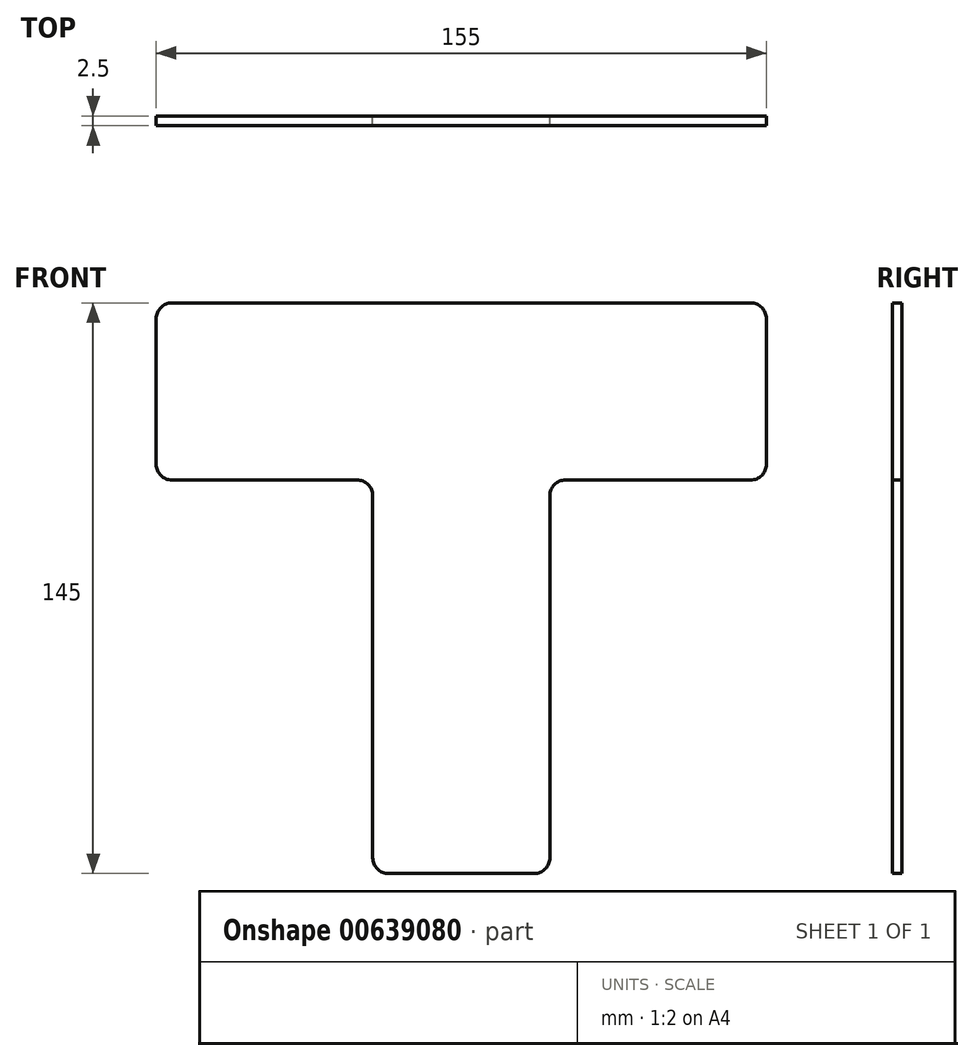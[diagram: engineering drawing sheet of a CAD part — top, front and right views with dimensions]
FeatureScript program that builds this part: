
annotation { "Feature Type Name" : "Feature", "Feature Type Description" : "" }
export const myFeature = defineFeature(function(context is Context, id is Id, definition is map)
    precondition{}
    {
        {
            var Q0;
            Q0=qCreatedBy(makeId("Front.planeOp"),FACE);
            var sketch = newSketch(context, id + "F0", { "sketchPlane" : qUnion([Q0])});
            skLineSegment(sketch, "E0.bottom", {"start": v(73.5, 22.5) * mm, "end": v(-73.5, 22.5) * mm});
            skLineSegment(sketch, "E0.top", {"start": v(77.5, -22.5) * mm, "end": v(22.5, -22.5) * mm});
            skLineSegment(sketch, "E0.left", {"start": v(77.5, 18.5) * mm, "end": v(77.5, -18.5) * mm});
            skLineSegment(sketch, "E0.right", {"start": v(-77.5, 18.5) * mm, "end": v(-77.5, -18.5) * mm});
            skPoint(sketch, "E0.middle", {"position": v(0, 0) * mm});
            skLineSegment(sketch, "E1", {"start": v(73.5, -22.5) * mm, "end": v(26.5, -22.5) * mm});
            skLineSegment(sketch, "E2", {"start": v(22.5, -26.5) * mm, "end": v(22.5, -118.5) * mm});
            skLineSegment(sketch, "E3", {"start": v(18.5, -122.5) * mm, "end": v(-18.5, -122.5) * mm});
            skLineSegment(sketch, "E4", {"start": v(-22.5, -118.5) * mm, "end": v(-22.5, -26.5) * mm});
            skLineSegment(sketch, "E5", {"start": v(-22.5, -22.5) * mm, "end": v(-77.5, -22.5) * mm});
            skLineSegment(sketch, "E6.trimOffspring", {"start": v(-26.5, -22.5) * mm, "end": v(-73.5, -22.5) * mm});
            skPoint(sketch, "E7.visualSharp", {"position": v(-77.5, 22.5) * mm});
            skArc(sketch, "E7.filletArc", {"start": v(-73.5, 22.5) * mm, "mid": v(-76.33, 21.33) * mm, "end": v(-77.5, 18.5) * mm});
            skPoint(sketch, "E8.visualSharp", {"position": v(-77.5, -22.5) * mm});
            skArc(sketch, "E8.filletArc", {"start": v(-77.5, -18.5) * mm, "mid": v(-76.33, -21.33) * mm, "end": v(-73.5, -22.5) * mm});
            skPoint(sketch, "E9.visualSharp", {"position": v(77.5, -22.5) * mm});
            skArc(sketch, "E9.filletArc", {"start": v(73.5, -22.5) * mm, "mid": v(76.33, -21.33) * mm, "end": v(77.5, -18.5) * mm});
            skPoint(sketch, "E10.visualSharp", {"position": v(77.5, 22.5) * mm});
            skArc(sketch, "E10.filletArc", {"start": v(77.5, 18.5) * mm, "mid": v(76.33, 21.33) * mm, "end": v(73.5, 22.5) * mm});
            skPoint(sketch, "E11.visualSharp", {"position": v(22.5, -22.5) * mm});
            skArc(sketch, "E11.filletArc", {"start": v(26.5, -22.5) * mm, "mid": v(23.67, -23.67) * mm, "end": v(22.5, -26.5) * mm});
            skPoint(sketch, "E12.visualSharp", {"position": v(-22.5, -22.5) * mm});
            skArc(sketch, "E12.filletArc", {"start": v(-22.5, -26.5) * mm, "mid": v(-23.67, -23.67) * mm, "end": v(-26.5, -22.5) * mm});
            skPoint(sketch, "E13.visualSharp", {"position": v(-22.5, -122.5) * mm});
            skArc(sketch, "E13.filletArc", {"start": v(-22.5, -118.5) * mm, "mid": v(-21.33, -121.33) * mm, "end": v(-18.5, -122.5) * mm});
            skPoint(sketch, "E14.visualSharp", {"position": v(22.5, -122.5) * mm});
            skArc(sketch, "E14.filletArc", {"start": v(18.5, -122.5) * mm, "mid": v(21.33, -121.33) * mm, "end": v(22.5, -118.5) * mm});
            skSolve(sketch);
        }
        {
            var Q0;
            Q0 = qSketchRegion(id + "F0", true);
            extrude(context, id + "F1", {"entities" : qUnion([Q0]), "depth" : 2.5 * mm, "offsetDistance" : 25 * mm});
        }
    });
